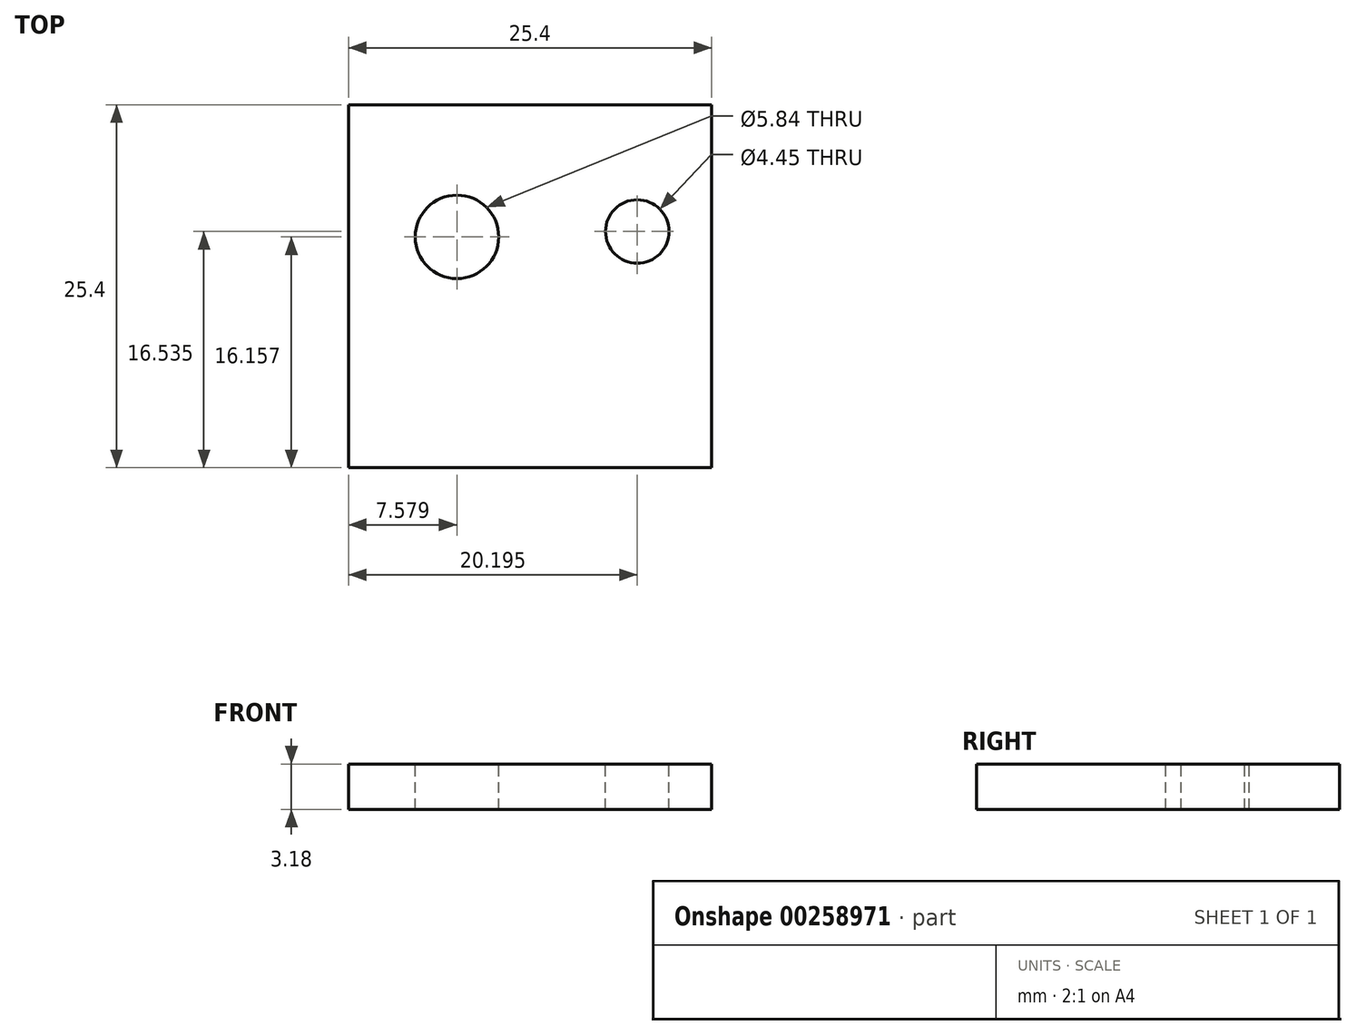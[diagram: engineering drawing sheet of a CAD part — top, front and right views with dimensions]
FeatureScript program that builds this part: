
annotation { "Feature Type Name" : "Feature", "Feature Type Description" : "" }
export const myFeature = defineFeature(function(context is Context, id is Id, definition is map)
    precondition{}
    {
        {
            var Q0;
            Q0=qCreatedBy(makeId("Top.planeOp"),FACE);
            var sketch = newSketch(context, id + "F0", { "sketchPlane" : qUnion([Q0])});
            skLineSegment(sketch, "E0.bottom", {"start": v(-16.83, 15.89) * mm, "end": v(8.57, 15.89) * mm});
            skLineSegment(sketch, "E0.top", {"start": v(-16.83, -9.51) * mm, "end": v(8.57, -9.51) * mm});
            skLineSegment(sketch, "E0.left", {"start": v(-16.83, 15.89) * mm, "end": v(-16.83, -9.51) * mm});
            skLineSegment(sketch, "E0.right", {"start": v(8.57, 15.89) * mm, "end": v(8.57, -9.51) * mm});
            skCircle(sketch, "E1", {"center": v(-9.25, 6.65) * mm, "radius": 2.92 * mm});
            skCircle(sketch, "E2", {"center": v(3.36, 7.03) * mm, "radius": 2.22 * mm});
            skSolve(sketch);
        }
        {
            var Q0;
            Q0=makeQuery(id+"F0.imprint","IMPRINT",FACE,{"disambiguationData":[TD([[makeQuery(id+"F0.imprint","IMPRINT",EDGE,{"derivedFrom":sQuery(id+"F0.wireOp",EDGE,"E0.bottom")}),-1.0]])]});
            var Q1;
            Q1=makeQuery(id+"F0.imprint","IMPRINT",FACE,{"disambiguationData":[TD([[makeQuery(id+"F0.imprint","IMPRINT",EDGE,{"derivedFrom":sQuery(id+"F0.wireOp",EDGE,"mxrBNE5u-oahF-ZrPX-VrP8-rVD9jizwPYgD.bottom")}),-1.0]])]});
            extrude(context, id + "F1", {"entities" : qUnion([Q0, Q1]), "oppositeDirection" : true, "depth" : 3.17 * mm});
        }
    });
